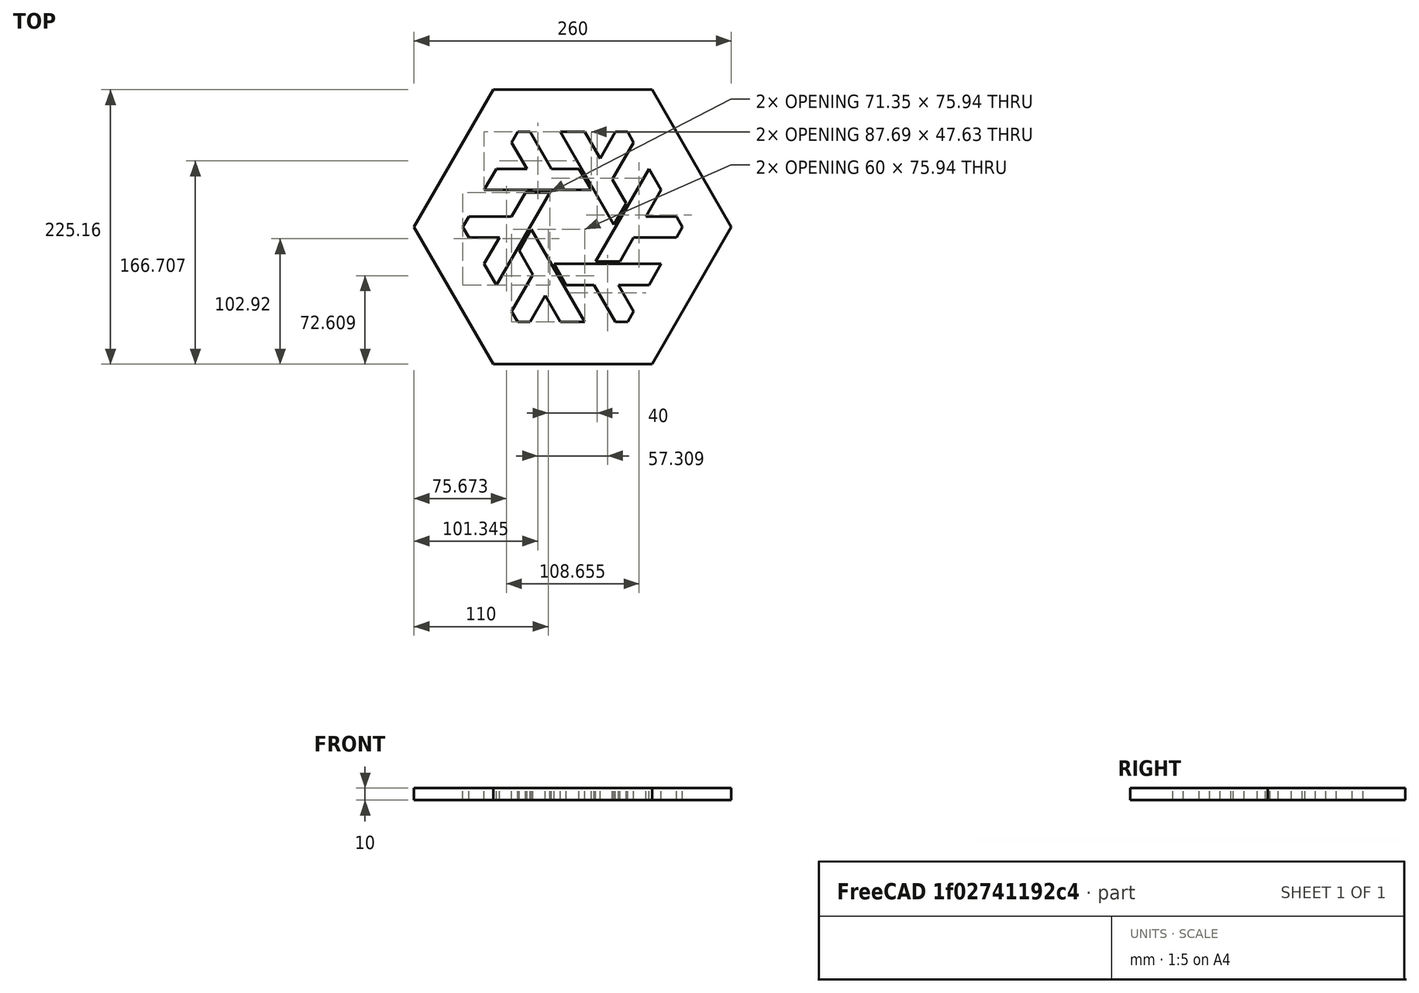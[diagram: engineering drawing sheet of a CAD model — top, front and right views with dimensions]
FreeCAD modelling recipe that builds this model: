
FCSTD DOCUMENT  (FreeCAD 1.0RUnknown)
Label: nixos-cad
License: All rights reserved
LicenseURL: http://en.wikipedia.org/wiki/All_rights_reserved
objects: TechDraw::DrawViewDimension×6, Sketcher::SketchObject×1, PartDesign::Pad×1, PartDesign::Body×1, TechDraw::DrawSVGTemplate×1, TechDraw::DrawProjGroupItem×1, TechDraw::DrawPage×1
note: 15 computed .brp shape members not serialized (recipe doc carries the construction recipe); baked Part::Feature solids carry a one-line shape summary decoded from their .brp

FEATURE [Sketcher::SketchObject] Sketch
  ArcFitTolerance = 1e-06
  AttachmentSupport = -> [XY_Plane]
  FullyConstrained = true
  MakeInternals = false
  MapMode = 5
  sketch-geometry (96):
    g0: LineSegment [constr] StartX=90 StartY=0 StartZ=0 EndX=45 EndY=77.9423 EndZ=0
    g1: LineSegment [constr] StartX=45 StartY=77.9423 StartZ=0 EndX=-45 EndY=77.9423 EndZ=0
    g2: LineSegment [constr] StartX=-45 StartY=77.9423 StartZ=0 EndX=-90 EndY=-5.68e-14 EndZ=0
    g3: LineSegment [constr] StartX=-90 StartY=-5.15e-14 StartZ=0 EndX=-45 EndY=-77.9423 EndZ=0
    g4: LineSegment [constr] StartX=45 StartY=-77.9423 StartZ=0 EndX=90 EndY=0 EndZ=0
    g5: Circle [constr] CenterX=0 CenterY=0 CenterZ=0 NormalX=0 NormalY=0 NormalZ=1 AngleXU=0 Radius=90
    g6: GeomPoint X=-35 Y=77.9423 Z=0
    g7: GeomPoint X=-10 Y=77.9423 Z=0
    g8: GeomPoint X=10 Y=77.9423 Z=0
    g9: GeomPoint X=35 Y=77.9423 Z=0
    g10: GeomPoint X=-35 Y=-77.9423 Z=0
    g11: GeomPoint X=-10 Y=-77.9423 Z=0
    g12: GeomPoint X=10 Y=-77.9423 Z=0
    g13: GeomPoint X=35 Y=-77.9423 Z=0
    g14: GeomPoint X=-50 Y=69.282 Z=0
    g15: GeomPoint X=-62.5 Y=47.6314 Z=0
    g16: GeomPoint X=-72.5 Y=30.3109 Z=0
    g17: GeomPoint X=-85 Y=-8.66025 Z=0
    g18: GeomPoint X=-72.5 Y=-30.3109 Z=0
    g19: GeomPoint X=-62.5 Y=-47.6314 Z=0
    g20: GeomPoint X=-50 Y=-69.282 Z=0
    g21: GeomPoint X=62.5 Y=-47.6314 Z=0
    g22: GeomPoint X=72.5 Y=-30.3109 Z=0
    g23: GeomPoint X=85 Y=-8.66025 Z=0
    g24: GeomPoint X=72.5 Y=30.3109 Z=0
    g25: GeomPoint X=62.5 Y=47.6314 Z=0
    g26: GeomPoint X=50 Y=69.282 Z=0
    g27: LineSegment StartX=35 StartY=77.9423 StartZ=0 EndX=22.5 EndY=56.2917 EndZ=0
    g28: LineSegment StartX=10 StartY=77.9423 StartZ=0 EndX=22.5 EndY=56.2917 EndZ=0
    g29: LineSegment StartX=50 StartY=69.282 StartZ=0 EndX=32.5 EndY=38.9711 EndZ=0
    g30: LineSegment StartX=32.5 StartY=38.9711 StartZ=0 EndX=43.8453 EndY=19.3205 EndZ=0
    g31: LineSegment StartX=43.8453 StartY=19.3205 StartZ=0 EndX=33.8453 EndY=2 EndZ=0
    g32: LineSegment StartX=33.8453 StartY=2 StartZ=0 EndX=-10 EndY=77.9423 EndZ=0
    g33: LineSegment StartX=-10 StartY=77.9423 StartZ=0 EndX=10 EndY=77.9423 EndZ=0
    g34: LineSegment StartX=35 StartY=77.9423 StartZ=0 EndX=45 EndY=77.9423 EndZ=0
    g35: LineSegment StartX=45 StartY=77.9423 StartZ=0 EndX=50 EndY=69.282 EndZ=0
    g36: LineSegment [constr] StartX=22.5 StartY=56.2917 StartZ=0 EndX=32.5 EndY=38.9711 EndZ=0
    g37: LineSegment StartX=85 StartY=-8.66025 StartZ=0 EndX=50 EndY=-8.66025 EndZ=0
    g38: LineSegment StartX=50 StartY=-8.66025 StartZ=0 EndX=38.6547 EndY=-28.3109 EndZ=0
    g39: LineSegment StartX=38.6547 StartY=-28.3109 StartZ=0 EndX=18.6547 EndY=-28.3109 EndZ=0
    g40: LineSegment StartX=18.6547 StartY=-28.3109 StartZ=0 EndX=62.5 EndY=47.6314 EndZ=0
    g41: LineSegment StartX=62.5 StartY=47.6314 StartZ=0 EndX=72.5 EndY=30.3109 EndZ=0
    g42: LineSegment StartX=72.5 StartY=30.3109 StartZ=0 EndX=60 EndY=8.66025 EndZ=0
    g43: LineSegment StartX=60 StartY=8.66025 StartZ=0 EndX=85 EndY=8.66025 EndZ=0
    g44: LineSegment StartX=85 StartY=8.66025 StartZ=0 EndX=90 EndY=0 EndZ=0
    g45: LineSegment StartX=90 StartY=0 StartZ=0 EndX=85 EndY=-8.66025 EndZ=0
    g46: LineSegment [constr] StartX=60 StartY=8.66025 StartZ=0 EndX=50 EndY=-8.66025 EndZ=0
    g47: LineSegment StartX=35 StartY=-77.9423 StartZ=0 EndX=17.5 EndY=-47.6314 EndZ=0
    g48: LineSegment StartX=17.5 StartY=-47.6314 StartZ=0 EndX=-5.1906 EndY=-47.6314 EndZ=0
    g49: LineSegment StartX=-5.1906 StartY=-47.6314 StartZ=0 EndX=-15.1906 EndY=-30.3109 EndZ=0
    g50: LineSegment StartX=-15.1906 StartY=-30.3109 StartZ=0 EndX=72.5 EndY=-30.3109 EndZ=0
    g51: LineSegment StartX=72.5 StartY=-30.3109 StartZ=0 EndX=62.5 EndY=-47.6314 EndZ=0
    g52: LineSegment StartX=62.5 StartY=-47.6314 StartZ=0 EndX=37.5 EndY=-47.6314 EndZ=0
    g53: LineSegment StartX=37.5 StartY=-47.6314 StartZ=0 EndX=50 EndY=-69.282 EndZ=0
    g54: LineSegment StartX=50 StartY=-69.282 StartZ=0 EndX=45 EndY=-77.9423 EndZ=0
    g55: LineSegment StartX=45 StartY=-77.9423 StartZ=0 EndX=35 EndY=-77.9423 EndZ=0
    g56: LineSegment [constr] StartX=37.5 StartY=-47.6314 StartZ=0 EndX=17.5 EndY=-47.6314 EndZ=0
    g57: LineSegment StartX=-85 StartY=-8.66025 StartZ=0 EndX=-60 EndY=-8.66025 EndZ=0
    g58: LineSegment StartX=-60 StartY=-8.66025 StartZ=0 EndX=-72.5 EndY=-30.3109 EndZ=0
    g59: LineSegment StartX=-72.5 StartY=-30.3109 StartZ=0 EndX=-62.5 EndY=-47.6314 EndZ=0
    g60: LineSegment StartX=-62.5 StartY=-47.6314 StartZ=0 EndX=-18.6547 EndY=28.3109 EndZ=0
    g61: LineSegment StartX=-18.6547 StartY=28.3109 StartZ=0 EndX=-38.6547 EndY=28.3109 EndZ=0
    g62: LineSegment StartX=-38.6547 StartY=28.3109 StartZ=0 EndX=-50 EndY=8.66025 EndZ=0
    g63: LineSegment StartX=-50 StartY=8.66025 StartZ=0 EndX=-85 EndY=8.66025 EndZ=0
    g64: LineSegment StartX=-85 StartY=8.66025 StartZ=0 EndX=-90 EndY=-5.15e-14 EndZ=0
    g65: LineSegment StartX=-90 StartY=-5.15e-14 StartZ=0 EndX=-85 EndY=-8.66025 EndZ=0
    g66: LineSegment StartX=-50 StartY=69.282 StartZ=0 EndX=-45 EndY=77.9423 EndZ=0
    g67: LineSegment StartX=-45 StartY=77.9423 StartZ=0 EndX=-35 EndY=77.9423 EndZ=0
    g68: LineSegment StartX=-35 StartY=77.9423 StartZ=0 EndX=-17.5 EndY=47.6314 EndZ=0
    g69: LineSegment StartX=-17.5 StartY=47.6314 StartZ=0 EndX=5.1906 EndY=47.6314 EndZ=0
    g70: LineSegment StartX=5.1906 StartY=47.6314 StartZ=0 EndX=15.1906 EndY=30.3109 EndZ=0
    g71: LineSegment StartX=15.1906 StartY=30.3109 StartZ=0 EndX=-72.5 EndY=30.3109 EndZ=0
    g72: LineSegment StartX=-72.5 StartY=30.3109 StartZ=0 EndX=-62.5 EndY=47.6314 EndZ=0
    g73: LineSegment StartX=-62.5 StartY=47.6314 StartZ=0 EndX=-37.5 EndY=47.6314 EndZ=0
    g74: LineSegment StartX=-37.5 StartY=47.6314 StartZ=0 EndX=-50 EndY=69.282 EndZ=0
    g75: LineSegment StartX=-35 StartY=-77.9423 StartZ=0 EndX=-22.5 EndY=-56.2917 EndZ=0
    g76: LineSegment StartX=-22.5 StartY=-56.2917 StartZ=0 EndX=-10 EndY=-77.9423 EndZ=0
    g77: LineSegment StartX=-10 StartY=-77.9423 StartZ=0 EndX=10 EndY=-77.9423 EndZ=0
    g78: LineSegment StartX=10 StartY=-77.9423 StartZ=0 EndX=-33.8453 EndY=-2 EndZ=0
    g79: LineSegment StartX=-33.8453 StartY=-2 StartZ=0 EndX=-43.8453 EndY=-19.3205 EndZ=0
    g80: LineSegment StartX=-43.8453 StartY=-19.3205 StartZ=0 EndX=-32.5 EndY=-38.9711 EndZ=0
    g81: LineSegment StartX=-32.5 StartY=-38.9711 StartZ=0 EndX=-50 EndY=-69.282 EndZ=0
    g82: LineSegment StartX=-50 StartY=-69.282 StartZ=0 EndX=-45 EndY=-77.9423 EndZ=0
    g83: LineSegment StartX=-45 StartY=-77.9423 StartZ=0 EndX=-35 EndY=-77.9423 EndZ=0
    g84: LineSegment [constr] StartX=-60 StartY=-8.66025 StartZ=0 EndX=-50 EndY=8.66025 EndZ=0
    g85: LineSegment [constr] StartX=-32.5 StartY=-38.9711 StartZ=0 EndX=-22.5 EndY=-56.2917 EndZ=0
    g86: LineSegment [constr] StartX=-37.5 StartY=47.6314 StartZ=0 EndX=-17.5 EndY=47.6314 EndZ=0
    g87: LineSegment [constr] StartX=-35 StartY=-77.9423 StartZ=0 EndX=-10 EndY=-77.9423 EndZ=0
    g88: LineSegment [constr] StartX=10 StartY=-77.9423 StartZ=0 EndX=35 EndY=-77.9423 EndZ=0
    g89: LineSegment StartX=130 StartY=0 StartZ=0 EndX=65 EndY=112.583 EndZ=0
    g90: LineSegment StartX=65 StartY=112.583 StartZ=0 EndX=-65 EndY=112.583 EndZ=0
    g91: LineSegment StartX=-65 StartY=112.583 StartZ=0 EndX=-130 EndY=-2.84e-14 EndZ=0
    g92: LineSegment StartX=-130 StartY=-2.84e-14 StartZ=0 EndX=-65 EndY=-112.583 EndZ=0
    g93: LineSegment StartX=-65 StartY=-112.583 StartZ=0 EndX=65 EndY=-112.583 EndZ=0
    g94: LineSegment StartX=65 StartY=-112.583 StartZ=0 EndX=130 EndY=0 EndZ=0
    g95: Circle [constr] CenterX=0 CenterY=0 CenterZ=0 NormalX=0 NormalY=0 NormalZ=1 AngleXU=0 Radius=130
  constraints (228):
    c: Coincident(g0,g1)
    c: Coincident(g1,g2)
    c: Coincident(g2,g3)
    c: Coincident(g4,g0)
    c: Equal(g0,g1)
    c: Equal(g0,g3)
    c: Equal(g0,g4)
    c: PointOnObject(g0,g5)
    c: PointOnObject(g1,g5)
    c: PointOnObject(g2,g5)
    c: PointOnObject(g3,g5)
    c: PointOnObject(g4,g5)
    c: PointOnObject(g4,g5)
    c: Coincident(g5,g-1)
    c: PointOnObject(g4,g-1)
    c: PointOnObject(g6,g1)
    c: PointOnObject(g7,g1)
    c: PointOnObject(g8,g1)
    c: PointOnObject(g9,g1)
    c: DistanceX(g9,g0) = 10
    c: DistanceX(g8,g9) = 25
    c: DistanceX(g7,g8) = 20
    c: DistanceX(g6,g7) = 25
    c: DistanceX(g1,g6) = 10
    c: Vertical(g9,g13)
    c: Vertical(g8,g12)
    c: Vertical(g7,g11)
    c: Vertical(g6,g10)
    c: PointOnObject(g14,g2)
    c: PointOnObject(g15,g2)
    c: PointOnObject(g16,g2)
    c: PointOnObject(g17,g3)
    c: PointOnObject(g18,g3)
    c: PointOnObject(g19,g3)
    c: PointOnObject(g20,g3)
    c: PointOnObject(g21,g4)
    c: PointOnObject(g22,g4)
    c: PointOnObject(g23,g4)
    c: PointOnObject(g24,g0)
    c: PointOnObject(g25,g0)
    c: PointOnObject(g26,g0)
    c: Distance(g0,g0) = 90
    c: Coincident(g27,g9)
    c: Coincident(g28,g8)
    c: Coincident(g28,g27)
    c: Coincident(g29,g26)
    c: Coincident(g29,g30)
    c: Coincident(g30,g31)
    c: Coincident(g31,g32)
    c: Coincident(g32,g7)
    c: Coincident(g32,g33)
    c: Coincident(g33,g8)
    c: Horizontal(g33)
    c: Coincident(g34,g9)
    c: Coincident(g34,g0)
    c: Coincident(g34,g35)
    c: Coincident(g35,g26)
    c: Parallel(g28,g32)
    c: Parallel(g30,g32)
    c: Parallel(g29,g27)
    c: Coincident(g36,g27)
    c: Coincident(g36,g29)
    c: Parallel(g36,g28)
    c: Coincident(g37,g23)
    c: Horizontal(g37)
    c: Coincident(g37,g38)
    c: Coincident(g38,g39)
    c: Coincident(g39,g40)
    c: Coincident(g40,g25)
    c: Coincident(g40,g41)
    c: Coincident(g41,g24)
    c: Coincident(g41,g42)
    c: Coincident(g42,g43)
    c: PointOnObject(g43,g0)
    c: Horizontal(g43)
    c: Coincident(g43,g44)
    c: Coincident(g44,g0)
    c: Coincident(g44,g45)
    c: Coincident(g45,g37)
    c: Parallel(g31,g40)
    c: Parallel(g38,g40)
    c: Parallel(g42,g40)
    c: Coincident(g46,g42)
    c: Coincident(g46,g37)
    c: Parallel(g46,g38)
    c: Coincident(g47,g13)
    c: Coincident(g47,g48)
    c: Horizontal(g48)
    c: Coincident(g48,g49)
    c: Coincident(g49,g50)
    c: Coincident(g50,g22)
    c: Horizontal(g50)
    c: Coincident(g50,g51)
    c: Coincident(g51,g21)
    c: Coincident(g51,g52)
    c: Coincident(g52,g53)
    c: PointOnObject(g53,g4)
    c: Coincident(g53,g54)
    c: Coincident(g54,g55)
    c: Coincident(g55,g13)
    c: Parallel(g39,g50)
    c: Coincident(g56,g52)
    c: Coincident(g56,g47)
    c: Parallel(g56,g48)
    c: Parallel(g52,g56)
    c: Coincident(g57,g17)
    c: Coincident(g57,g58)
    c: Coincident(g58,g18)
    c: Coincident(g58,g59)
    c: Coincident(g59,g19)
    c: Coincident(g59,g60)
    c: Coincident(g60,g61)
    c: Coincident(g61,g62)
    c: Coincident(g62,g63)
    c: PointOnObject(g63,g2)
    c: Horizontal(g63)
    c: Coincident(g63,g64)
    c: Coincident(g64,g2)
    c: Coincident(g64,g65)
    c: Coincident(g65,g57)
    c: Coincident(g66,g14)
    c: Coincident(g66,g1)
    c: Coincident(g66,g67)
    c: Coincident(g67,g6)
    c: Coincident(g67,g68)
    c: Coincident(g68,g69)
    c: Coincident(g69,g70)
    c: Coincident(g70,g71)
    c: Coincident(g71,g16)
    c: Coincident(g71,g72)
    c: Coincident(g72,g15)
    c: Coincident(g72,g73)
    c: Coincident(g73,g74)
    c: Coincident(g74,g66)
    c: Coincident(g75,g10)
    c: Coincident(g75,g76)
    c: Coincident(g76,g11)
    c: Coincident(g76,g77)
    c: Coincident(g77,g12)
    c: Coincident(g77,g78)
    c: Coincident(g78,g79)
    c: Coincident(g79,g80)
    c: Coincident(g80,g81)
    c: Coincident(g81,g20)
    c: Coincident(g81,g82)
    c: Coincident(g82,g3)
    c: Coincident(g82,g83)
    c: Coincident(g83,g75)
    c: Coincident(g84,g57)
    c: Coincident(g84,g62)
    c: Coincident(g85,g80)
    c: Coincident(g85,g75)
    c: Coincident(g86,g73)
    c: Coincident(g86,g68)
    c: Parallel(g74,g68)
    c: Parallel(g63,g57)
    c: Parallel(g81,g75)
    c: Parallel(g62,g84)
    c: Parallel(g80,g85)
    c: Parallel(g76,g85)
    c: Parallel(g62,g60)
    c: Parallel(g58,g60)
    c: Parallel(g73,g71)
    c: Parallel(g86,g71)
    c: Parallel(g69,g71)
    c: Equal(g67,g66)
    c: Equal(g66,g64)
    c: Equal(g64,g65)
    c: Equal(g65,g82)
    c: Equal(g55,g54)
    c: Equal(g54,g44)
    c: Equal(g44,g45)
    c: Equal(g35,g34)
    c: Parallel(g79,g60)
    c: Parallel(g71,g61)
    c: Parallel(g49,g78)
    c: Parallel(g70,g32)
    c: Equal(g40,g50)
    c: Equal(g50,g78)
    c: Equal(g78,g60)
    c: Equal(g60,g71)
    c: Equal(g28,g27)
    c: Equal(g27,g74)
    c: Equal(g74,g73)
    c: Equal(g73,g57)
    c: Equal(g57,g58)
    c: Equal(g58,g75)
    c: Equal(g75,g76)
    c: Equal(g76,g53)
    c: Equal(g53,g52)
    c: Equal(g52,g43)
    c: Equal(g43,g42)
    c: Equal(g70,g31)
    c: Equal(g31,g39)
    c: Equal(g39,g49)
    c: Equal(g49,g79)
    c: Equal(g79,g61)
    c: Coincident(g87,g10)
    c: Coincident(g87,g11)
    c: Horizontal(g87)
    c: Coincident(g88,g12)
    c: Coincident(g88,g13)
    c: Parallel(g88,g77)
    c: Parallel(g77,g87)
    c: Parallel(g83,g87)
    c: Equal(g83,g82)
    c: Coincident(g54,g4)
    c: Equal(g72,g33)
    c: Equal(g59,g77)
    c: DistanceY(g22,g38) = 2
    c: Equal(g47,g37)
    c: Equal(g30,g38)
    c: Coincident(g89,g90)
    c: Coincident(g90,g91)
    c: Coincident(g91,g92)
    c: Coincident(g92,g93)
    c: Coincident(g93,g94)
    c: Coincident(g94,g89)
    c: Equal(g89, g90-g94) x5
    c: PointOnObject(g89,g95)
    c: PointOnObject(g90,g95)
    c: PointOnObject(g91,g95)
    c: PointOnObject(g92,g95)
    c: PointOnObject(g93,g95)
    c: PointOnObject(g94,g95)
    c: Coincident(g95,g5)
    c: PointOnObject(g94,g-1)
    c: DistanceX(g0,g89) = 40
FEATURE [PartDesign::Pad] Pad
  Direction = (0,0,1)
  Length = 10
  Length2 = 10
  Profile = -> Sketch
  ReferenceAxis = -> Sketch [N_Axis]
  Refine = true
  Suppressed = false
  Type = 0
FEATURE [PartDesign::Body] Body
  AllowCompound = false
  Group = -> [Sketch,Pad]
  Origin = -> Origin
  Tip = -> Pad
FEATURE [TechDraw::DrawSVGTemplate] Template
  EditableTexts = approval_person=<owner>; creator=<owner>; date_of_issue=23/11/2024; document_type=Assembly Drawing; general_tolerances=ISO 2768-m; identification_number=1; language_code=EN; part_material=Stainless steel Mat.No. 1.4301; revision_index=AAA; sheet_number=1 / 1; sheet_scale=1 : 1; title=nixos-cad
  Height = 297
  Orientation = 1
  Template = /nix/store/34wrskp4kcm2yi9kl0nzkspyglyk6ac7-freecad-1.0rc2/share/Mod/TechDraw/Templates/A3_Landscape_ISO5457_minimal.svg
  Width = 420
FEATURE [TechDraw::DrawProjGroupItem] View  label="rstrst"
  CoarseView = false
  Direction = (0,0,1)
  Focus = 100
  HardHidden = false
  IsoCount = 0
  IsoHidden = false
  IsoVisible = false
  LockPosition = false
  Perspective = false
  Rotation = 0
  RotationVector = (1,0,0)
  ScaleType = 0
  ScrubCount = 1
  SeamHidden = false
  SeamVisible = false
  SmoothHidden = false
  SmoothVisible = true
  Source = -> [Pad]
  Type = 0
  X = 153.126
  XDirection = (1,0,0)
  Y = 148.623
FEATURE [TechDraw::DrawViewDimension] Dimension
  AngleOverride = false
  Arbitrary = false
  ArbitraryTolerances = false
  BoxCorners = (2) [(-130,-112.583,0),(130,112.583,0)]
  EqualTolerance = true
  ExtensionAngle = 0
  FormatSpec = %.2w
  FormatSpecOverTolerance = %+.2w
  FormatSpecUnderTolerance = %+.2w
  Inverted = false
  LineAngle = 0
  LockPosition = false
  MeasureType = 1
  OverTolerance = 0
  References2D = -> [View]
  Rotation = 0
  ScaleType = 0
  TheoreticalExact = false
  Type = 0
  UnderTolerance = 0
  X = 40
  Y = 104.775
FEATURE [TechDraw::DrawViewDimension] Dimension001
  AngleOverride = false
  Arbitrary = false
  ArbitraryTolerances = false
  BoxCorners = (2) [(-130,-112.583,0),(130,112.583,0)]
  EqualTolerance = true
  ExtensionAngle = 0
  FormatSpec = %.2w
  FormatSpecOverTolerance = %+.2w
  FormatSpecUnderTolerance = %+.2w
  Inverted = false
  LineAngle = 0
  LockPosition = false
  MeasureType = 1
  OverTolerance = 0
  References2D = -> [View]
  Rotation = 0
  ScaleType = 0
  TheoreticalExact = false
  Type = 1
  UnderTolerance = 0
  X = 22.5
  Y = 104.775
FEATURE [TechDraw::DrawViewDimension] Dimension002
  AngleOverride = false
  Arbitrary = false
  ArbitraryTolerances = false
  BoxCorners = (2) [(-130,-112.583,0),(130,112.583,0)]
  EqualTolerance = true
  ExtensionAngle = 0
  FormatSpec = %.2w
  FormatSpecOverTolerance = %+.2w
  FormatSpecUnderTolerance = %+.2w
  Inverted = false
  LineAngle = 0
  LockPosition = false
  MeasureType = 1
  OverTolerance = 0
  References2D = -> [View]
  Rotation = 0
  ScaleType = 0
  TheoreticalExact = false
  Type = 1
  UnderTolerance = 0
  X = 0
  Y = 104.775
FEATURE [TechDraw::DrawViewDimension] Dimension003
  AngleOverride = false
  Arbitrary = false
  ArbitraryTolerances = false
  BoxCorners = (2) [(-130,-112.583,0),(130,112.583,0)]
  EqualTolerance = true
  ExtensionAngle = 0
  FormatSpec = %.2w
  FormatSpecOverTolerance = %+.2w
  FormatSpecUnderTolerance = %+.2w
  Inverted = false
  LineAngle = 0
  LockPosition = false
  MeasureType = 1
  OverTolerance = 0
  References2D = -> [View]
  Rotation = 0
  ScaleType = 0
  TheoreticalExact = false
  Type = 1
  UnderTolerance = 0
  X = -26.0349
  Y = 104.775
FEATURE [TechDraw::DrawViewDimension] Dimension004
  AngleOverride = false
  Arbitrary = false
  ArbitraryTolerances = false
  BoxCorners = (2) [(-190,-164.545,0),(190,164.545,0)]
  EqualTolerance = true
  ExtensionAngle = 0
  FormatSpec = %.2w
  FormatSpecOverTolerance = %+.2w
  FormatSpecUnderTolerance = %+.2w
  Inverted = false
  LineAngle = 0
  LockPosition = false
  MeasureType = 1
  OverTolerance = 0
  References2D = -> [View]
  Rotation = 0
  ScaleType = 0
  TheoreticalExact = false
  Type = 0
  UnderTolerance = 0
  X = -40
  Y = 104.775
FEATURE [TechDraw::DrawViewDimension] Dimension005
  AngleOverride = false
  Arbitrary = false
  ArbitraryTolerances = false
  BoxCorners = (2) [(-190,-164.545,0),(190,164.545,0)]
  EqualTolerance = true
  ExtensionAngle = 0
  FormatSpec = %.2w
  FormatSpecOverTolerance = %+.2w
  FormatSpecUnderTolerance = %+.2w
  Inverted = false
  LineAngle = 0
  LockPosition = false
  MeasureType = 1
  OverTolerance = 0
  References2D = -> [View]
  Rotation = 0
  ScaleType = 0
  TheoreticalExact = false
  Type = 2
  UnderTolerance = 0
  X = 95.6239
  Y = -9.72149
FEATURE [TechDraw::DrawPage] Page
  KeepUpdated = true
  NextBalloonIndex = 1
  ProjectionType = 0
  Template = -> Template
  Views = -> [View,Dimension,Dimension001,Dimension002,Dimension003,Dimension004,Dimension005]
